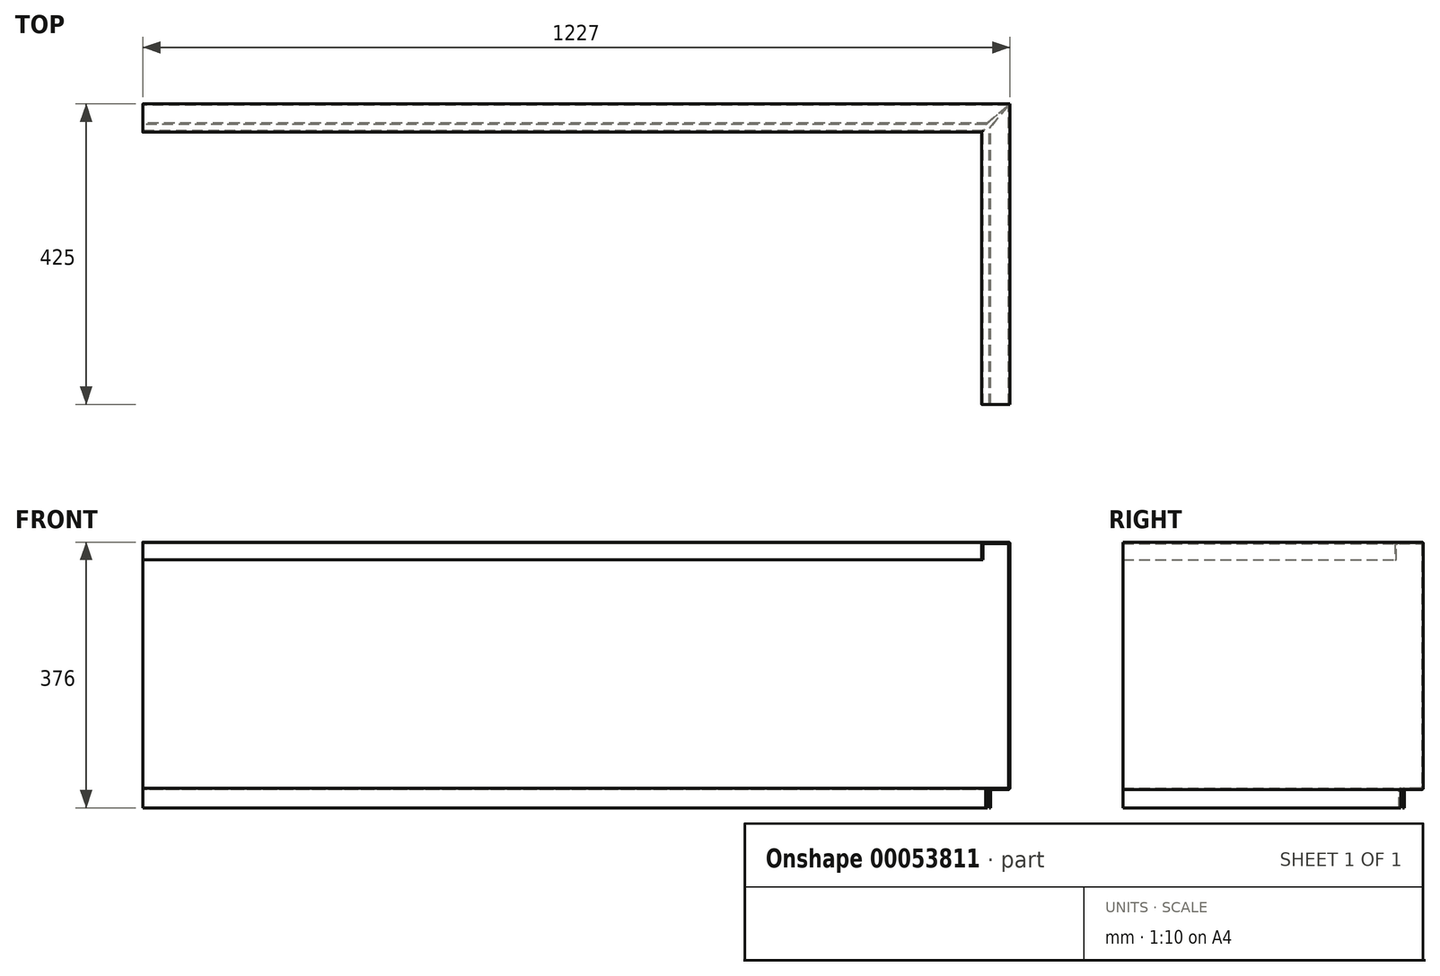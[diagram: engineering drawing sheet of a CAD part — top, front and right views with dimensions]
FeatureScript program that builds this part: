
annotation { "Feature Type Name" : "Feature", "Feature Type Description" : "" }
export const myFeature = defineFeature(function(context is Context, id is Id, definition is map)
    precondition{}
    {
        {
            var Q0;
            Q0=qCreatedBy(makeId("Front.planeOp"),FACE);
            var sketch = newSketch(context, id + "F0", { "sketchPlane" : qUnion([Q0])});
            skLineSegment(sketch, "E0", {"start": v(0, 0) * mm, "end": v(0, -350) * mm});
            skLineSegment(sketch, "E1", {"start": v(0, -350) * mm, "end": v(-27, -350) * mm});
            skLineSegment(sketch, "E2", {"start": v(-27, -350) * mm, "end": v(-27, -376) * mm});
            skLineSegment(sketch, "E3", {"start": v(0, 0) * mm, "end": v(-40, 0) * mm});
            skLineSegment(sketch, "E4", {"start": v(-40, 0) * mm, "end": v(-40, -25) * mm});
            skLineSegment(sketch, "E5.0", {"start": v(-38, -2) * mm, "end": v(-38, -25) * mm});
            skLineSegment(sketch, "E5.1", {"start": v(-29, -348) * mm, "end": v(-29, -376) * mm});
            skLineSegment(sketch, "E5.2", {"start": v(-2, -348) * mm, "end": v(-29, -348) * mm});
            skLineSegment(sketch, "E5.3", {"start": v(-2, -2) * mm, "end": v(-2, -348) * mm});
            skLineSegment(sketch, "E5.4", {"start": v(-2, -2) * mm, "end": v(-38, -2) * mm});
            skLineSegment(sketch, "E6", {"start": v(-40, -25) * mm, "end": v(-38, -25) * mm});
            skLineSegment(sketch, "E7", {"start": v(-29, -376) * mm, "end": v(-27, -376) * mm});
            skSolve(sketch);
        }
        {
            var Q0;
            Q0=qCreatedBy(makeId("Top.planeOp"),FACE);
            var sketch = newSketch(context, id + "F1", { "sketchPlane" : qUnion([Q0])});
            skLineSegment(sketch, "E8", {"start": v(0, 0) * mm, "end": v(0, 425) * mm});
            skLineSegment(sketch, "E9", {"start": v(-1227, 425) * mm, "end": v(0, 425) * mm});
            skSolve(sketch);
        }
        {
            var Q0;
            Q0=qSketchRegion(id+"F0",true);
            var Q1;
            Q1=qConstructionFilter(qBodyType(qCreatedBy(id+"F1",EDGE),BodyType.WIRE),ConstructionObject.NO);
            sweep(context, id + "F2", {"profiles" : qUnion([Q0]), "path" : qUnion([Q1])});
        }
        {
            var Q0;
            Q0=makeQuery(id+"F2.opSweep","SWEPT_FACE",FACE,{"disambiguationData":[OSD([sQuery(id+"F0.wireOp",EDGE,"E5.2"),sQuery(id+"F1.wireOp",EDGE,"E8")])]});
            var sketch = newSketch(context, id + "F3", { "sketchPlane" : qUnion([Q0])});
            skLineSegment(sketch, "E10", {"start": v(-2, 423) * mm, "end": v(-34.18, 396) * mm});
            skLineSegment(sketch, "E11", {"start": v(-34.18, 396) * mm, "end": v(-29, 390.82) * mm});
            skLineSegment(sketch, "E12", {"start": v(-29, 390.82) * mm, "end": v(-2, 423) * mm});
            skSolve(sketch);
        }
        {
            var Q0;
            Q0 = qSketchRegion(id + "F3", true);
            extrude(context, id + "F4", {"entities" : qUnion([Q0]), "operationType" : NewBodyOperationType.REMOVE, "oppositeDirection" : true, "depth" : 30 * mm});
        }
        {
            var Q0;
            Q0=makeQuery(id+"F2.opSweep","SWEPT_EDGE",EDGE,{"disambiguationData":[OSD([sQuery(id+"F0.wireOp",EDGE,"E5.1"),sQuery(id+"F0.wireOp",EDGE,"E5.2"),sQuery(id+"F1.wireOp",EDGE,"E9")])]});
            var Q1;
            Q1=makeQuery(id+"F2.opSweep","SWEPT_EDGE",EDGE,{"disambiguationData":[OSD([sQuery(id+"F0.wireOp",EDGE,"E5.2"),sQuery(id+"F0.wireOp",EDGE,"E5.3"),sQuery(id+"F1.wireOp",EDGE,"E9")])]});
            var Q2;
            Q2=makeQuery(id+"F2.opSweep","SWEPT_EDGE",EDGE,{"disambiguationData":[OSD([sQuery(id+"F0.wireOp",EDGE,"E3"),sQuery(id+"F0.wireOp",EDGE,"E4"),sQuery(id+"F1.wireOp",EDGE,"E9")])]});
            var Q3;
            Q3=makeQuery(id+"F2.opSweep","SWEPT_EDGE",EDGE,{"disambiguationData":[OSD([sQuery(id+"F0.wireOp",EDGE,"E0"),sQuery(id+"F0.wireOp",EDGE,"E3"),sQuery(id+"F1.wireOp",EDGE,"E9")])]});
            var Q4;
            Q4=makeQuery(id+"F2.opSweep","SWEPT_EDGE",EDGE,{"disambiguationData":[OSD([sQuery(id+"F0.wireOp",EDGE,"E0"),sQuery(id+"F0.wireOp",EDGE,"E3"),sQuery(id+"F1.wireOp",EDGE,"E8")])]});
            var Q5;
            Q5=makeQuery(id+"F2.opSweep","SWEPT_EDGE",EDGE,{"disambiguationData":[OSD([sQuery(id+"F0.wireOp",EDGE,"E3"),sQuery(id+"F0.wireOp",EDGE,"E4"),sQuery(id+"F1.wireOp",EDGE,"E8")])]});
            var Q6;
            Q6=makeQuery(id+"F2.opSweep","SWEPT_EDGE",EDGE,{"disambiguationData":[OSD([sQuery(id+"F0.wireOp",EDGE,"E5.2"),sQuery(id+"F0.wireOp",EDGE,"E5.3"),sQuery(id+"F1.wireOp",EDGE,"E8")])]});
            var Q7;
            Q7=makeQuery(id+"F2.opSweep","SWEPT_EDGE",EDGE,{"disambiguationData":[OSD([sQuery(id+"F0.wireOp",EDGE,"E5.1"),sQuery(id+"F0.wireOp",EDGE,"E5.2"),sQuery(id+"F1.wireOp",EDGE,"E8")])]});
            var Q8;
            Q8=makeQuery(id+"F2.opSweep","SWEPT_EDGE",EDGE,{"disambiguationData":[OSD([sQuery(id+"F0.wireOp",EDGE,"E1"),sQuery(id+"F0.wireOp",EDGE,"E2"),sQuery(id+"F1.wireOp",EDGE,"E9")])]});
            var Q9;
            Q9=makeQuery(id+"F2.opSweep","SWEPT_EDGE",EDGE,{"disambiguationData":[OSD([sQuery(id+"F0.wireOp",EDGE,"E0"),sQuery(id+"F0.wireOp",EDGE,"E1"),sQuery(id+"F1.wireOp",EDGE,"E9")])]});
            var Q10;
            Q10=makeQuery(id+"F2.opSweep","SWEPT_EDGE",EDGE,{"disambiguationData":[OSD([sQuery(id+"F0.wireOp",EDGE,"E5.0"),sQuery(id+"F0.wireOp",EDGE,"E5.4"),sQuery(id+"F1.wireOp",EDGE,"E9")])]});
            var Q11;
            Q11=makeQuery(id+"F2.opSweep","SWEPT_EDGE",EDGE,{"disambiguationData":[OSD([sQuery(id+"F0.wireOp",EDGE,"E5.3"),sQuery(id+"F0.wireOp",EDGE,"E5.4"),sQuery(id+"F1.wireOp",EDGE,"E9")])]});
            var Q12;
            Q12=makeQuery(id+"F2.opSweep","SWEPT_EDGE",EDGE,{"disambiguationData":[OSD([sQuery(id+"F0.wireOp",EDGE,"E5.0"),sQuery(id+"F0.wireOp",EDGE,"E5.4"),sQuery(id+"F1.wireOp",EDGE,"E8")])]});
            var Q13;
            Q13=makeQuery(id+"F2.opSweep","SWEPT_EDGE",EDGE,{"disambiguationData":[OSD([sQuery(id+"F0.wireOp",EDGE,"E5.3"),sQuery(id+"F0.wireOp",EDGE,"E5.4"),sQuery(id+"F1.wireOp",EDGE,"E8")])]});
            var Q14;
            Q14=makeQuery(id+"F2.opSweep","SWEPT_EDGE",EDGE,{"disambiguationData":[OSD([sQuery(id+"F0.wireOp",EDGE,"E0"),sQuery(id+"F0.wireOp",EDGE,"E1"),sQuery(id+"F1.wireOp",EDGE,"E8")])]});
            var Q15;
            Q15=makeQuery(id+"F2.opSweep","SWEPT_EDGE",EDGE,{"disambiguationData":[OSD([sQuery(id+"F0.wireOp",EDGE,"E1"),sQuery(id+"F0.wireOp",EDGE,"E2"),sQuery(id+"F1.wireOp",EDGE,"E8")])]});
            fillet(context, id + "F5", {"entities" : qUnion([Q0, Q1, Q2, Q3, Q4, Q5, Q6, Q7, Q8, Q9, Q10, Q11, Q12, Q13, Q14, Q15]), "radius" : 2 * mm, "tangentPropagation" : true, "allowEdgeOverflow" : false});
        }
    });
